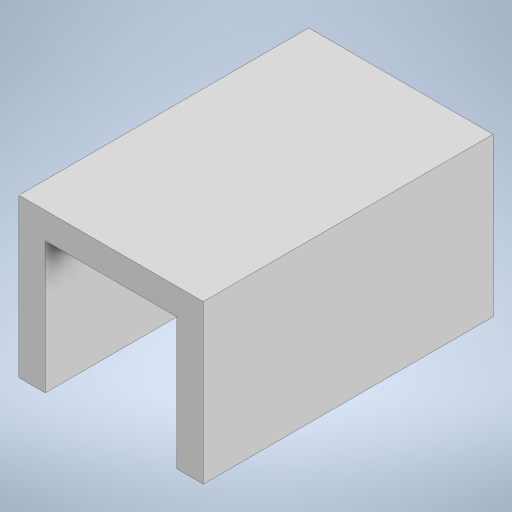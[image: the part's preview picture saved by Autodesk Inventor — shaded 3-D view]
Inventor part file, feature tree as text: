
AUTODESK INVENTOR PART (.ipt)
format: ipt  version: 2023 (Build 270158000, 158)  size: 184,320 bytes
history: native  units: in
note: dims shown in document units (in); Inventor stores cm internally (conversion verified against a paired STEP export)
features: sketch x6, extrude x3
ambient origin geometry x8: Origin, YZ Plane, XZ Plane, XY Plane, X Axis, Y Axis, Z Axis, Center Point
bodies: Solid1 (feature_tree)
feature tree (9):
  extrude  "Extrusion1"  Depth=0.4724in
  extrude  "Extrusion2"  Depth=0.3937in
  sketch  "Sketch8"  dims[d5=0.7874in d6=0.7874in d7=0.0in]
  sketch  "Sketch9"  dims[d24=0.1575in]
  sketch  "Sketch11"  dims[d25=0.3937in d26=0.0in]
  extrude  "Extrusion8"  Depth=0.7874in TaperAngle=0.0deg
  sketch  "Sketch1"  dims[d0=0.5512in d1=0.4724in]
  sketch  "Sketch2"  dims[d2=0.8661in d3=0.0in d4=0.3937in]
  sketch  "Sketch12"
